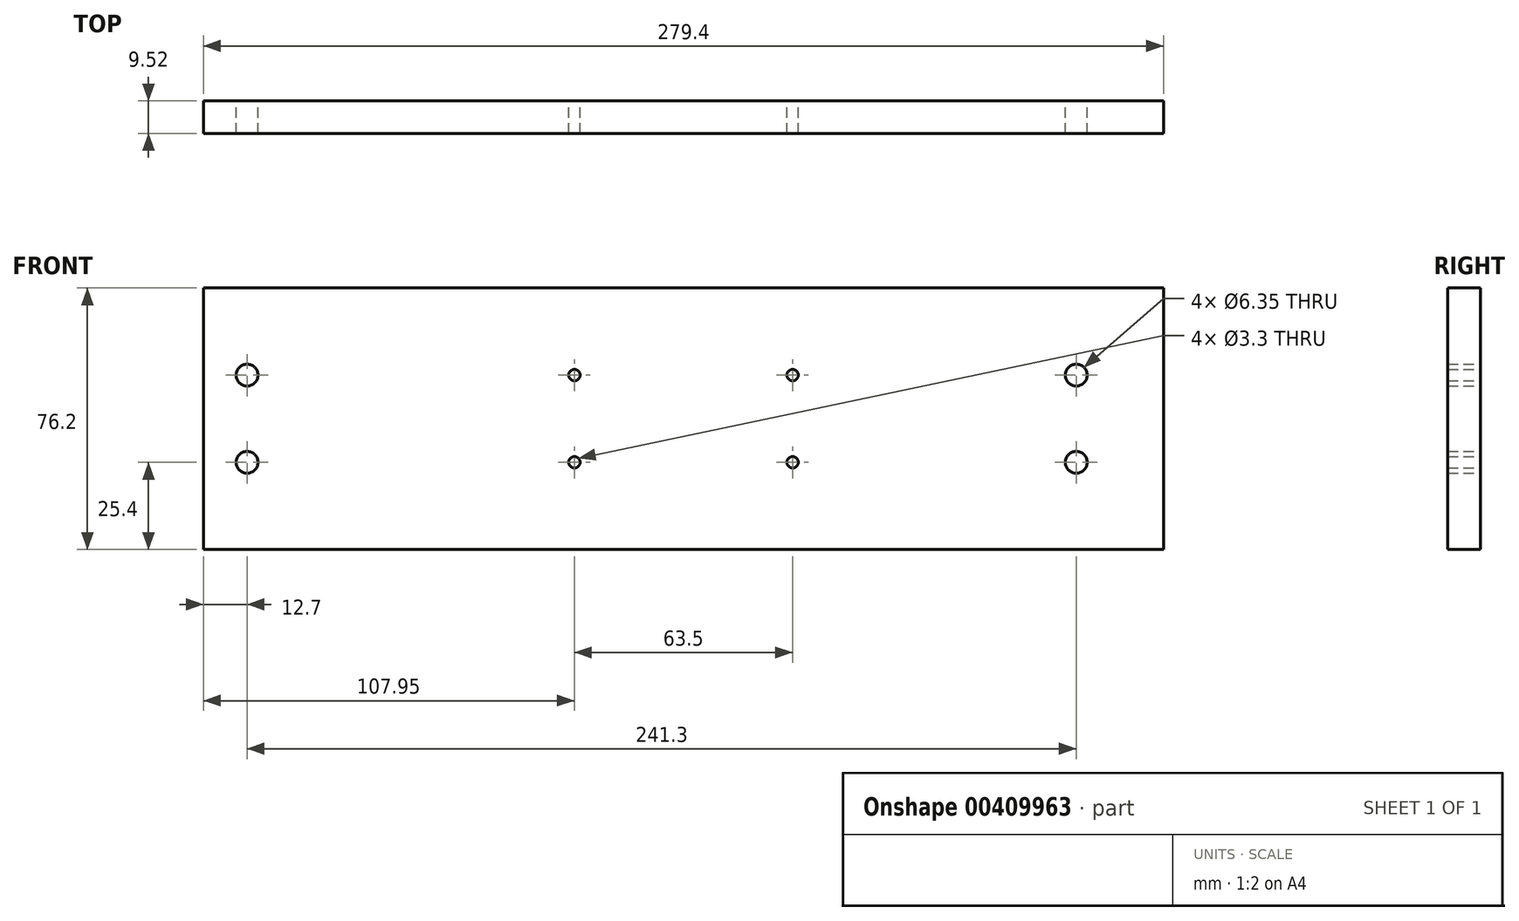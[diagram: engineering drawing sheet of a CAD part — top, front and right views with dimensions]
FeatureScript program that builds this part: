
annotation { "Feature Type Name" : "Feature", "Feature Type Description" : "" }
export const myFeature = defineFeature(function(context is Context, id is Id, definition is map)
    precondition{}
    {
        {
            var Q0;
            Q0=qCreatedBy(makeId("Front.planeOp"),FACE);
            var sketch = newSketch(context, id + "F0", { "sketchPlane" : qUnion([Q0])});
            skLineSegment(sketch, "E0.bottom", {"start": v(-152.4, 38.1) * mm, "end": v(127, 38.1) * mm});
            skLineSegment(sketch, "E0.top", {"start": v(-152.4, -38.1) * mm, "end": v(127, -38.1) * mm});
            skLineSegment(sketch, "E0.left", {"start": v(-152.4, 38.1) * mm, "end": v(-152.4, -38.1) * mm});
            skLineSegment(sketch, "E0.right", {"start": v(127, 38.1) * mm, "end": v(127, -38.1) * mm});
            skLineSegment(sketch, "E1", {"start": v(0, 75.12) * mm, "end": v(0, -82.9) * mm, "construction": true});
            skLineSegment(sketch, "E2", {"start": v(-184.13, 0) * mm, "end": v(223.98, 0) * mm, "construction": true});
            skLineSegment(sketch, "E3", {"start": v(-189.92, 12.7) * mm, "end": v(211.77, 12.7) * mm, "construction": true});
            skLineSegment(sketch, "E4", {"start": v(-196.4, -12.7) * mm, "end": v(209.42, -12.7) * mm, "construction": true});
            skCircle(sketch, "E5", {"center": v(-139.7, 12.7) * mm, "radius": 3.18 * mm});
            skCircle(sketch, "E6", {"center": v(-139.7, -12.7) * mm, "radius": 3.18 * mm});
            skLineSegment(sketch, "E7", {"start": v(-139.7, 78.39) * mm, "end": v(-139.7, -53.36) * mm, "construction": true});
            skLineSegment(sketch, "E8", {"start": v(-44.45, 63.97) * mm, "end": v(-44.45, -50.78) * mm, "construction": true});
            skLineSegment(sketch, "E9", {"start": v(19.05, 70.04) * mm, "end": v(19.05, -56.12) * mm, "construction": true});
            skLineSegment(sketch, "E10", {"start": v(101.6, 72.23) * mm, "end": v(101.6, -62.44) * mm, "construction": true});
            skCircle(sketch, "E11", {"center": v(-44.45, 12.7) * mm, "radius": 1.65 * mm});
            skCircle(sketch, "E12", {"center": v(-44.45, -12.7) * mm, "radius": 1.65 * mm});
            skCircle(sketch, "E13", {"center": v(19.05, 12.7) * mm, "radius": 1.65 * mm});
            skCircle(sketch, "E14", {"center": v(19.05, -12.7) * mm, "radius": 1.65 * mm});
            skCircle(sketch, "E15", {"center": v(101.6, -12.7) * mm, "radius": 3.18 * mm});
            skCircle(sketch, "E16", {"center": v(101.6, 12.7) * mm, "radius": 3.18 * mm});
            skSolve(sketch);
        }
        {
            var Q0;
            Q0 = qSketchRegion(id + "F0", true);
            extrude(context, id + "F1", {"entities" : qUnion([Q0]), "endBound" : BoundingType.SYMMETRIC, "depth" : 9.52 * mm});
        }
    });
